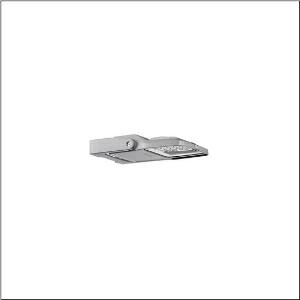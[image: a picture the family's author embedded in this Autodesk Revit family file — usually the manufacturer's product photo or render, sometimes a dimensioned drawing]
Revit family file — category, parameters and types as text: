
# Revit family: floodlight_fl_21_iq_micro___pl52_5xa7762a2d2a_5d06
name_source: partatom
category: Lighting Fixtures
units: mm (PartAtom-declared; Revit-internal decimal feet)

## family parameters
Cut with Voids When Loaded = No
Host = Face
Light Source = No
Part Type = Normal
Room Calculation Point = No
Round Connector Dimension = Use Diameter
Shared = No

## types (1)
- --- (1 x LED, 2890 lm, 23.1 W, 3000K)
    Apparent Load = 23 VA
    CIE Flux Codes = 26 60 98 100 100
    Color Rendering = 70
    Color Temperature = 3000K
    Default Elevation = 1800 mm
    Description = Floodlight FL 21 iQ micro, floodlight, primary light control with lens, of PMMA, primary optical cover: protective disc, of toughened safety glass, transparent, light distribution: PL52, light emission: direct distribution, installation type: surface-mounted, lamps: LED, High Power LED, rated values: 2.890lm | 23,1W | 125,1lm/W (begin service life); end service life: 2.890lm | 23,8W; at 50% lumin. flux: 1.445lm | 11W | 131,4lm/W, colour temperature: 3000K, colour rendering: CRI > 70, light colour: 730, light setting 1 begin service life: 100% | 2.890lm | 23,1W | 125,1lm/W | 3.000K, light setting 1 end service life: 23,8W, further light settings possible, control: Auto-Match, Temp-Guard, Night-Set, Smart-Wire, Desk-Remote (wireless, voltage-free reading and setting of iQ features in the workshop via application-optimized NFC function/RFID function), optimised constant luminous flux control (CLO 2.0), Street-Remote, with terminal, 6-pole, mains connection: 220..240V, AC, 50/60Hz, luminaire housing, of diecast aluminium, powder-coated, Siteco® metallic grey (DB 702S), corrosivity category C5 mid according to DIN EN ISO 12944suitable for swimming poolschlorine-resistant, sealing non-destructively replaceable, design bracket, of diecast aluminium, powder-coated, Siteco® metallic grey (DB 702S), protection rating (complete): IP66, insulation class (complete): insulation class II (safety insulation), certification: CE, ENEC, VDE, protection symbol: D, impact resistance: IK07, permissible operating ambient temperature: -40..+40°C, permissible operating ambient temperature for outdoor applications: -40..+50°C, standard: DIN EN 12944, LABS conformity tested according to VDMA 24364:2018-05, packaging unit: 1 piece

Light Distribution: PL52
    Height = 65 mm
    Lamp = 1 x LED
    Lamp Light Flux = 2890 lm
    Lamp Power = 23.1 W
    Lamp count = 1
    Length = 312 mm
    Luminous efficacy = 125 lm/W
    Manufacturer = Siteco
    ModVariant = No
    Model = 5XA7762A2D2A
    Mounting Place = Wall
    Mounting Type = Surface mounted
    Number of Poles = 1
    OnlyDefault = Yes
    Power Factor = 1
    Product Name = Floodlight FL 21 iQ micro | PL52
    Product group = floodlight | wall mounted
    ProductGroupID = 2002
    Protection Class = Protection class II
    Protection Degree = IP 66
    RLX_Detail_Level = 1
    RLX_Emergency_Light_Flux = 0 lm
    RLX_Emergency_Type = 0
    RLX_Emergency_Type_DB = No
    RlxData = <blob elided: 97773 chars, md5=455ae8ff>
    Socket = socket
    Standby Power = 0 W
    System Light Flux = 2890 lm
    System Power = 23 W
    Type Comments = factory setting: luminous flux: 100 % | dim-lin: 254 | 455 mA
    Type Image = l_1006878.jpg
    URL = http://relux.com
    VarID = @adj_181145
    Voltage = 0 V
    Weight = 0.00 kg
    Width = 230 mm

## geometry (parser evidence)
native form markers: Blend x4, Sweep x15
no freeform markers — native parametric forms only
